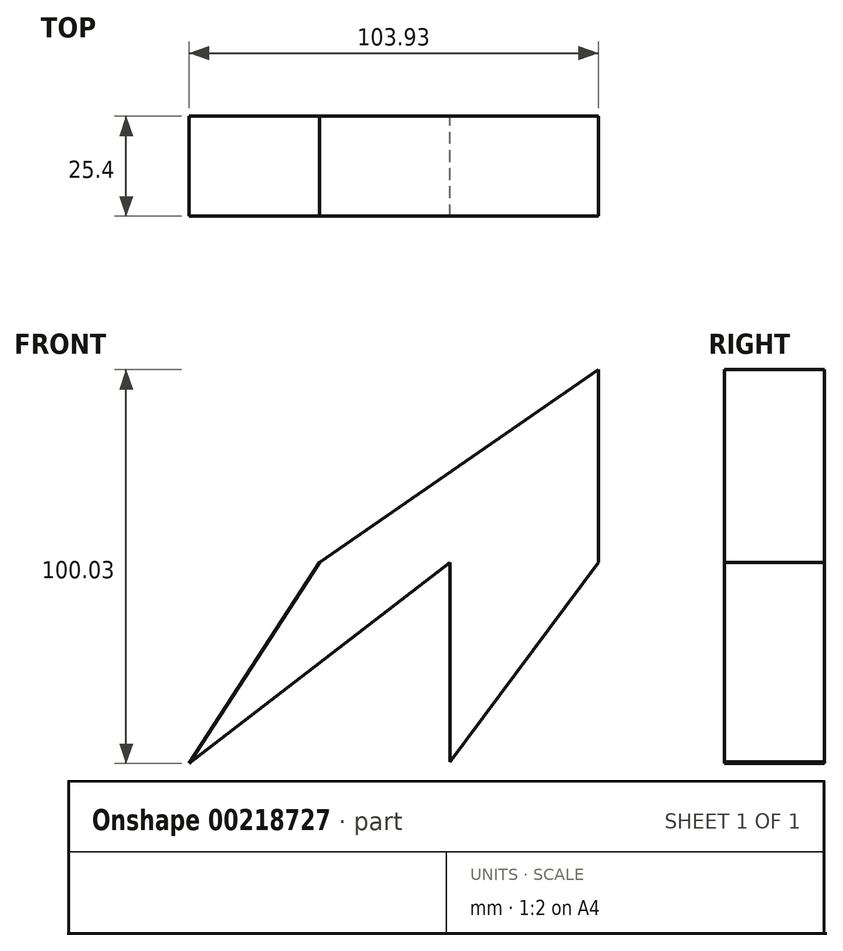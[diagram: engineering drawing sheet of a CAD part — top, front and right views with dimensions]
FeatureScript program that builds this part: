
annotation { "Feature Type Name" : "Feature", "Feature Type Description" : "" }
export const myFeature = defineFeature(function(context is Context, id is Id, definition is map)
    precondition{}
    {
        {
            var Q0;
            Q0=qCreatedBy(makeId("Front.planeOp"),FACE);
            var sketch = newSketch(context, id + "F0", { "sketchPlane" : qUnion([Q0])});
            skLineSegment(sketch, "E0", {"start": v(0, -50.7) * mm, "end": v(37.7, 0) * mm});
            skLineSegment(sketch, "E1", {"start": v(37.7, 0) * mm, "end": v(37.7, 48.94) * mm});
            skLineSegment(sketch, "E2", {"start": v(37.7, 48.94) * mm, "end": v(-33.11, 0) * mm});
            skLineSegment(sketch, "E3", {"start": v(-33.11, 0) * mm, "end": v(-66.23, -51.09) * mm});
            skLineSegment(sketch, "E4", {"start": v(-66.23, -51.09) * mm, "end": v(-33.11, 0) * mm});
            skLineSegment(sketch, "E5", {"start": v(0, 0) * mm, "end": v(0, -50.7) * mm});
            skLineSegment(sketch, "E6", {"start": v(0, 0) * mm, "end": v(-66.23, -51.09) * mm});
            skSolve(sketch);
        }
        {
            var Q0;
            Q0 = qSketchRegion(id + "F0", true);
            extrude(context, id + "F1", {"entities" : qUnion([Q0]), "depth" : 25.4 * mm});
        }
    });
